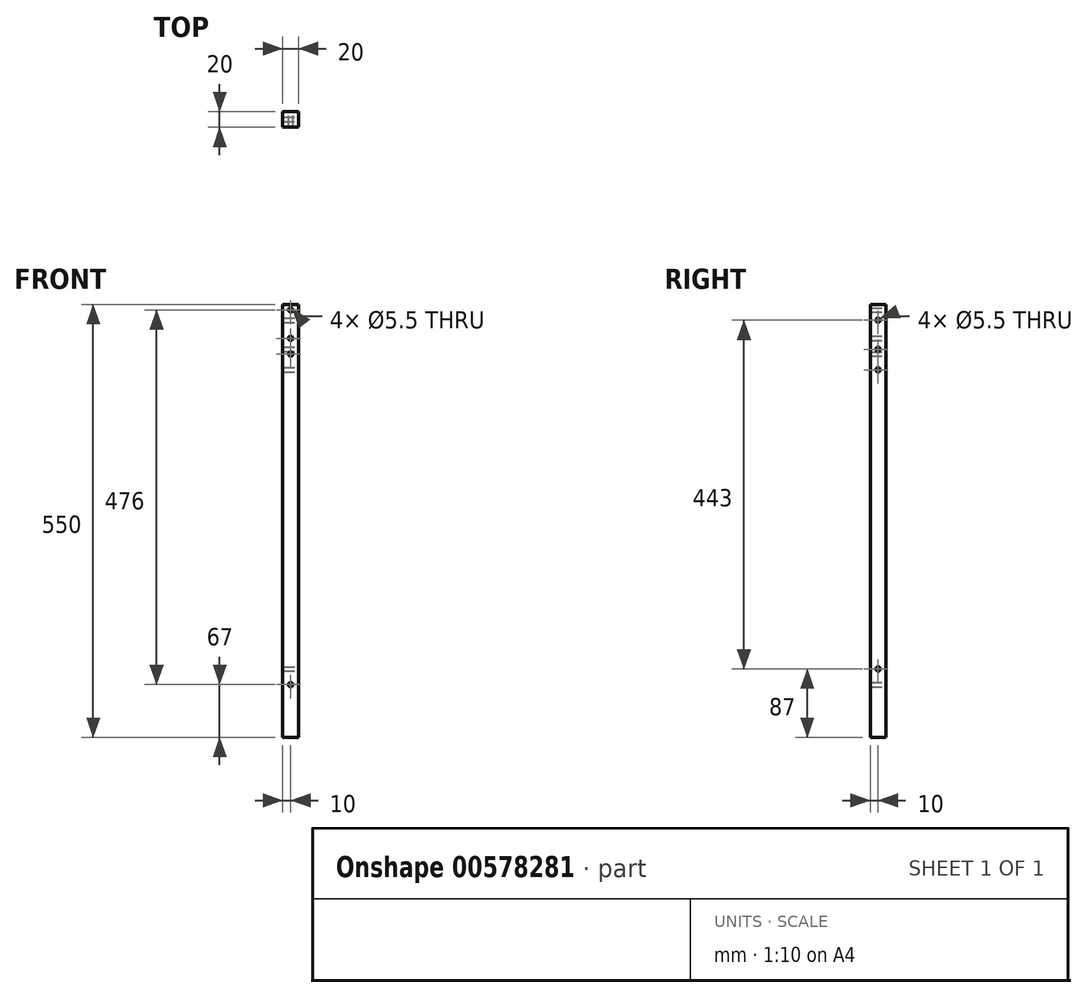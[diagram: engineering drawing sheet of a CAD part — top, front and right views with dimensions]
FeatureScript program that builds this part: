
annotation { "Feature Type Name" : "Feature", "Feature Type Description" : "" }
export const myFeature = defineFeature(function(context is Context, id is Id, definition is map)
    precondition{}
    {
        {
            var Q0;
            Q0=qCreatedBy(makeId("Front.planeOp"),FACE);
            var sketch = newSketch(context, id + "F0", { "sketchPlane" : qUnion([Q0])});
            skLineSegment(sketch, "E0", {"start": v(-10, 0) * mm, "end": v(10, 0) * mm});
            skLineSegment(sketch, "E1", {"start": v(10, 0) * mm, "end": v(10, 550) * mm});
            skLineSegment(sketch, "E2", {"start": v(10, 550) * mm, "end": v(-10, 550) * mm});
            skLineSegment(sketch, "E3", {"start": v(-10, 550) * mm, "end": v(-10, 0) * mm});
            skCircle(sketch, "E4", {"center": v(0, 543) * mm, "radius": 2.75 * mm});
            skPoint(sketch, "E4.centerSnap0", {"position": v(0, 550) * mm});
            skCircle(sketch, "E5", {"center": v(0, 507) * mm, "radius": 2.75 * mm});
            skCircle(sketch, "E6", {"center": v(0, 487) * mm, "radius": 2.75 * mm});
            skCircle(sketch, "E7", {"center": v(0, 67) * mm, "radius": 2.75 * mm});
            skSolve(sketch);
        }
        {
            var Q0;
            Q0 = qSketchRegion(id + "F0", true);
            extrude(context, id + "F1", {"entities" : qUnion([Q0]), "depth" : 20 * mm, "offsetDistance" : 25 * mm});
        }
        {
            var Q0;
            Q0=makeQuery(id+"F1.opExtrude","SWEPT_FACE",FACE,{"disambiguationData":[OSD([sQuery(id+"F0.wireOp",EDGE,"E1")])]});
            var sketch = newSketch(context, id + "F2", { "sketchPlane" : qUnion([Q0])});
            skCircle(sketch, "E8", {"center": v(-10, 530) * mm, "radius": 2.75 * mm});
            skPoint(sketch, "E8.centerSnap0", {"position": v(-10, 550) * mm});
            skCircle(sketch, "E9", {"center": v(-10, 493) * mm, "radius": 2.75 * mm});
            skCircle(sketch, "E10", {"center": v(-10, 467) * mm, "radius": 2.75 * mm});
            skCircle(sketch, "E11", {"center": v(-10, 87) * mm, "radius": 2.75 * mm});
            skSolve(sketch);
        }
        {
            var Q0;
            Q0 = qSketchRegion(id + "F2", true);
            extrude(context, id + "F3", {"entities" : qUnion([Q0]), "operationType" : NewBodyOperationType.REMOVE, "oppositeDirection" : true, "depth" : 20 * mm, "offsetDistance" : 25 * mm});
        }
    });
